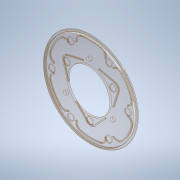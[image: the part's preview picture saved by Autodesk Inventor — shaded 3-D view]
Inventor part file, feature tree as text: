
AUTODESK INVENTOR PART (.ipt)
format: ipt  version: 2020 (Build 240168000, 168)  size: 426,496 bytes
history: native  units: in
note: dims shown in document units (in); Inventor stores cm internally (conversion verified against a paired STEP export)
features: sketch x13, extrude x10, projected_geometry x5, plane x2, shell x1, sweep x1, hole x1
ambient origin geometry x8: Origin, YZ Plane, XZ Plane, XY Plane, X Axis, Y Axis, Z Axis, Center Point
bodies: Solid1 (feature_tree)
feature tree (33):
  extrude  "Extrusion1"  Depth=3.1496in TaperAngle=0.0deg
  shell  "Shell1"  Thickness=0.1181in
  extrude  "Extrusion2"  Depth=3.1496in TaperAngle=0.0deg
  extrude  "Extrusion3"  Depth=1.5748in
  plane  "Work Plane1"
  extrude  "Extrusion4"  TaperAngle=120.0deg  [1 undecoded]
  extrude  "Extrusion5"  Depth=0.378in
  plane  "Work Plane4"
  sweep  "Sweep2"
  extrude  "Extrusion6"  [1 undecoded]
  hole  "Hole1"  [1 undecoded]
  extrude  "Extrusion9"  Depth=0.1181in TaperAngle=0.0deg
  extrude  "Extrusion10"  Depth=0.0591in
  extrude  "Extrusion11"  Depth=0.0591in
  extrude  "Extrusion12"  Depth=0.0591in
  sketch  "Sketch1"  dims[d1=5.3543in d2=3.1496in d3=0.0in d4=0.1181in]
  sketch  "Sketch2"  dims[d5=2.5197in d6=3.1496in d7=0.0in]
  sketch  "Sketch3"  dims[d8=0.378in d9=1.5748in]
  projected_geometry  "Projected Loop1"
  sketch  "Sketch4"  dims[d10=120.0deg d11=120.0deg]
  sketch  "Sketch6"  dims[d12=0.378in d13=0.378in]
  projected_geometry  "Projected Loop3"
  sketch  "Sketch9"  dims[d14=1.5748in d15=1.5748in]
  projected_geometry  "Projected Loop4"
  sketch  "Sketch10"  dims[d16=0.06in d17=0.0in d18=-0.9843in]
  sketch  "Sketch11"  dims[d24=1.1811in d25=0.9843in d26=0.0in]
  projected_geometry  "Projected Loop5"
  sketch  "Sketch14"  dims[d27=0.1181in d28=2.2201in d29=0.0in]
  sketch  "Sketch16"  dims[d37=0.0in d38=0.0in d39=0.0591in]
  sketch  "Sketch17"  dims[d40=0.0591in d41=0.0591in]
  projected_geometry  "Projected Loop7"
  sketch  "Sketch18"  dims[d42=0.0591in d43=0.0591in]
  sketch  "Sketch19"  dims[d44=0.0591in d45=0.0591in d46=0.9843in d47=0.9843in d48=0.9843in d49=0.9843in d50=0.9843in d51=0.9843in d52=0.0591in d53=0.0in d98=0.2362in d99=1.6142in d100=1.1811in d102=360.0deg d104=0.2362in d105=0.2362in d106=0.1575in d107=0.0787in d108=90.0deg d109=0.315in d110=0.8108in d111=0.3937in d112=0.0in d113=0.3937in d114=0.0in d115=5.5906in d116=0.378in d117=5.1181in d118=2.2638in d119=0.0591in d120=0.7874in d121=0.7874in d122=2.3622in d124=360.0deg d126=0.0591in d127=0.0591in d128=2.3622in d130=360.0deg d132=0.0591in d133=0.0in d134=0.378in d135=2.2638in d136=2.3622in d138=360.0deg d140=0.06in d141=0.0in]
note: 3 required parameter values undecoded (feature->parameter linkage not recoverable at this tier; creation-order binding heuristic only, values carry confidence <= 0.55)
